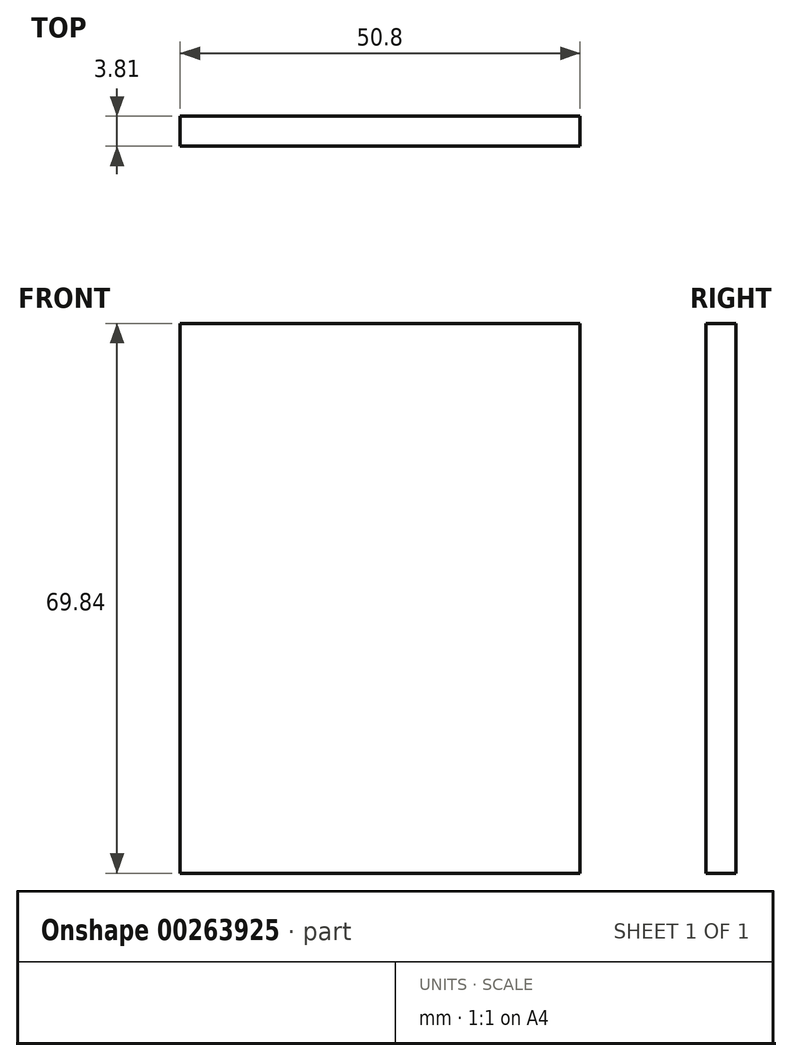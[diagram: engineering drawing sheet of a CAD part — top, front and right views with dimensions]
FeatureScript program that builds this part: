
annotation { "Feature Type Name" : "Feature", "Feature Type Description" : "" }
export const myFeature = defineFeature(function(context is Context, id is Id, definition is map)
    precondition{}
    {
        {
            var Q0;
            Q0=qCreatedBy(makeId("Front.planeOp"),FACE);
            var sketch = newSketch(context, id + "F0", { "sketchPlane" : qUnion([Q0])});
            skLineSegment(sketch, "E0.bottom", {"start": v(25.4, 34.93) * mm, "end": v(-25.4, 34.93) * mm});
            skLineSegment(sketch, "E0.top", {"start": v(25.4, -34.93) * mm, "end": v(-25.4, -34.93) * mm});
            skLineSegment(sketch, "E0.left", {"start": v(25.4, 34.93) * mm, "end": v(25.4, -34.93) * mm});
            skLineSegment(sketch, "E0.right", {"start": v(-25.4, 34.93) * mm, "end": v(-25.4, -34.93) * mm});
            skPoint(sketch, "E0.middle", {"position": v(0, 0) * mm});
            skSolve(sketch);
        }
        {
            var Q0;
            Q0=makeQuery(id+"F0.imprint","IMPRINT",FACE,{"disambiguationData":[TD([[makeQuery(id+"F0.imprint","IMPRINT",EDGE,{"derivedFrom":sQuery(id+"F0.wireOp",EDGE,"E0.bottom")}),1.0]])]});
            extrude(context, id + "F1", {"entities" : qUnion([Q0]), "depth" : 3.8 * mm});
        }
    });
